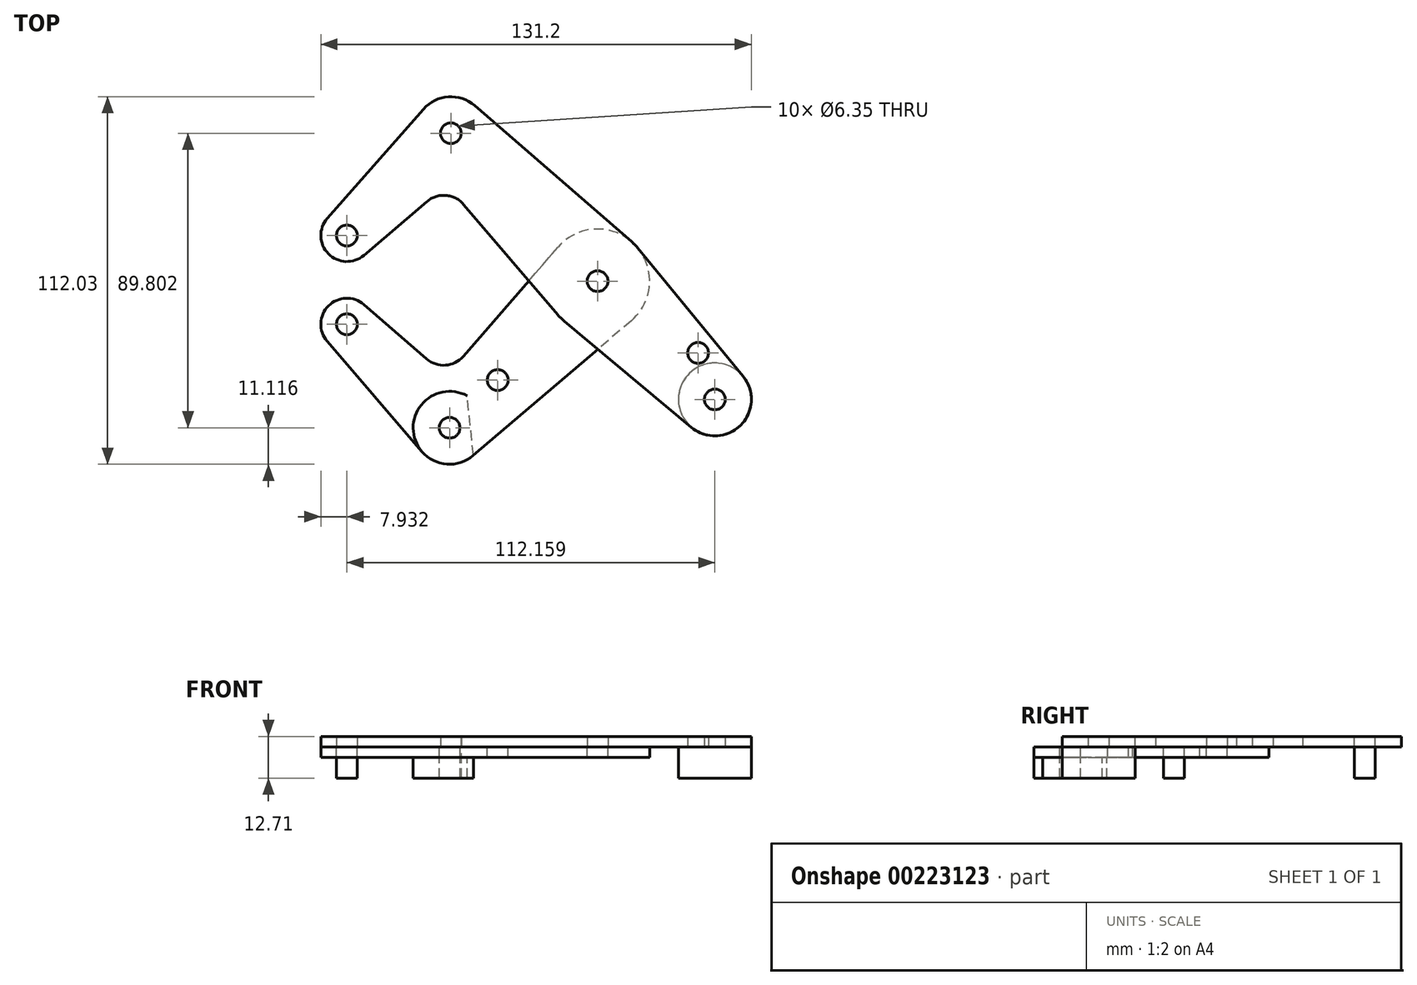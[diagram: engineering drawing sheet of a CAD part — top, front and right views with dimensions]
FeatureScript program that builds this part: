
annotation { "Feature Type Name" : "Feature", "Feature Type Description" : "" }
export const myFeature = defineFeature(function(context is Context, id is Id, definition is map)
    precondition{}
    {
        {
            var Q0;
            Q0=qCreatedBy(makeId("Top.planeOp"),FACE);
            var sketch = newSketch(context, id + "F0", { "sketchPlane" : qUnion([Q0])});
            skCircle(sketch, "E0", {"center": v(0, 0) * mm, "radius": 3.18 * mm});
            skCircle(sketch, "E1", {"center": v(0, 0) * mm, "radius": 3.98 * mm});
            skCircle(sketch, "E2", {"center": v(0, 0) * mm, "radius": 15.88 * mm});
            skCircle(sketch, "E3", {"center": v(35.77, -36.07) * mm, "radius": 11.11 * mm});
            skCircle(sketch, "E4", {"center": v(30.65, -21.9) * mm, "radius": 3.18 * mm});
            skCircle(sketch, "E5", {"center": v(-44.71, 45.09) * mm, "radius": 11.11 * mm});
            skCircle(sketch, "E6", {"center": v(-44.71, 45.09) * mm, "radius": 3.18 * mm});
            skCircle(sketch, "E7", {"center": v(-76.39, 13.9) * mm, "radius": 3.18 * mm});
            skCircle(sketch, "E8", {"center": v(-76.39, 13.9) * mm, "radius": 7.94 * mm});
            skCircle(sketch, "E9", {"center": v(-30.42, -30.17) * mm, "radius": 3.18 * mm});
            skCircle(sketch, "E10", {"center": v(-45.09, -44.71) * mm, "radius": 11.11 * mm});
            skCircle(sketch, "E11", {"center": v(-45.09, -44.71) * mm, "radius": 3.18 * mm});
            skCircle(sketch, "E12", {"center": v(-76.39, -13.15) * mm, "radius": 7.94 * mm});
            skCircle(sketch, "E13", {"center": v(-76.39, -13.15) * mm, "radius": 3.18 * mm});
            skLineSegment(sketch, "E14", {"start": v(-82.35, 19.14) * mm, "end": v(-53.06, 52.43) * mm});
            skLineSegment(sketch, "E15", {"start": v(-37.43, 53.48) * mm, "end": v(10.4, 12) * mm});
            skLineSegment(sketch, "E16", {"start": v(12.27, 10.07) * mm, "end": v(44.36, -29.02) * mm});
            skLineSegment(sketch, "E17", {"start": v(28.65, -44.6) * mm, "end": v(-10.17, -12.19) * mm});
            skLineSegment(sketch, "E18", {"start": v(10.3, -12.08) * mm, "end": v(-37.88, -53.17) * mm});
            skLineSegment(sketch, "E19", {"start": v(-40.89, -22.91) * mm, "end": v(-12, 10.4) * mm});
            skArc(sketch, "E20", {"start": v(-52, 24.26) * mm, "mid": v(-46.22, 26.14) * mm, "end": v(-40.8, 23.37) * mm});
            skLineSegment(sketch, "E21.trimOffspring", {"start": v(-40.8, 23.37) * mm, "end": v(-12.08, -10.3) * mm});
            skArc(sketch, "E22", {"start": v(-52.1, -23.7) * mm, "mid": v(-46.33, -25.63) * mm, "end": v(-40.89, -22.91) * mm});
            skLineSegment(sketch, "E23", {"start": v(0, 0) * mm, "end": v(-45.09, -44.71) * mm, "construction": true});
            skLineSegment(sketch, "E24", {"start": v(-45.09, -44.71) * mm, "end": v(-76.39, -13.15) * mm, "construction": true});
            skLineSegment(sketch, "E25", {"start": v(-44.71, 45.09) * mm, "end": v(-76.39, 13.9) * mm, "construction": true});
            skLineSegment(sketch, "E26", {"start": v(-76.39, 13.9) * mm, "end": v(-76.39, -13.15) * mm, "construction": true});
            skCircle(sketch, "E27", {"center": v(35.77, -36.07) * mm, "radius": 3.18 * mm});
            skLineSegment(sketch, "E28", {"start": v(-53.52, -51.96) * mm, "end": v(-82.4, -18.33) * mm});
            skLineSegment(sketch, "E29", {"start": v(-71.19, -7.16) * mm, "end": v(-52.1, -23.7) * mm});
            skLineSegment(sketch, "E30", {"start": v(-44.71, 45.09) * mm, "end": v(35.77, -36.07) * mm, "construction": true});
            skLineSegment(sketch, "E31", {"start": v(-52, 24.26) * mm, "end": v(-71.24, 7.86) * mm});
            skSolve(sketch);
        }
        {
            var Q0;
            {var subQ0=sQuery(id+"F0.wireOp",EDGE,"E14");Q0=makeQuery(id+"F0.imprint","IMPRINT",FACE,{"disambiguationData":[TD([[makeQuery(id+"F0.imprint","IMPRINT",EDGE,{"derivedFrom":subQ0}),-1.0]])]});}
            var Q1;
            Q1=makeQuery(id+"F0.imprint","IMPRINT",FACE,{"disambiguationData":[TD([[makeQuery(id+"F0.imprint","IMPRINT",EDGE,{"derivedFrom":sQuery(id+"F0.wireOp",EDGE,"E1")}),-1.0]])]});
            var Q2;
            Q2=makeQuery(id+"F0.imprint","IMPRINT",FACE,{"disambiguationData":[TD([[makeQuery(id+"F0.imprint","IMPRINT",EDGE,{"derivedFrom":sQuery(id+"F0.wireOp",EDGE,"E4")}),-1.0]])]});
            var Q3;
            Q3=makeQuery(id+"F0.imprint","IMPRINT",FACE,{"disambiguationData":[TD([[makeQuery(id+"F0.imprint","IMPRINT",EDGE,{"derivedFrom":sQuery(id+"F0.wireOp",EDGE,"E27")}),-1.0]])]});
            var Q4;
            Q4=makeQuery(id+"F0.imprint","IMPRINT",FACE,{"disambiguationData":[TD([[makeQuery(id+"F0.imprint","IMPRINT",EDGE,{"derivedFrom":sQuery(id+"F0.wireOp",EDGE,"E6")}),-1.0]])]});
            var Q5;
            Q5=makeQuery(id+"F0.imprint","IMPRINT",FACE,{"disambiguationData":[TD([[makeQuery(id+"F0.imprint","IMPRINT",EDGE,{"derivedFrom":sQuery(id+"F0.wireOp",EDGE,"E7")}),-1.0]])]});
            var Q6;
            {var subQ0=sQuery(id+"F0.wireOp",EDGE,"E19");var subQ1=sQuery(id+"F0.wireOp",EDGE,"E2");var subQ2=makeQuery(id+"F0.imprint","INTERSECT",VERTEX,{"derivedFrom":[subQ1,subQ0]});Q6=makeQuery(id+"F0.imprint","IMPRINT",FACE,{"disambiguationData":[TD([[makeQuery(id+"F0.imprint","IMPRINT",EDGE,{"disambiguationData":[TD([[subQ2,-1.0]])],"derivedFrom":subQ1}),-1.0]])]});}
            var Q7;
            {var subQ0=sQuery(id+"F0.wireOp",EDGE,"E17");var subQ1=sQuery(id+"F0.wireOp",EDGE,"E2");var subQ2=makeQuery(id+"F0.imprint","INTERSECT",VERTEX,{"derivedFrom":[subQ1,subQ0]});Q7=makeQuery(id+"F0.imprint","IMPRINT",FACE,{"disambiguationData":[TD([[makeQuery(id+"F0.imprint","IMPRINT",EDGE,{"disambiguationData":[TD([[subQ2,-1.0]])],"derivedFrom":subQ1}),-1.0]])]});}
            var Q8;
            Q8=makeQuery(id+"F0.imprint","IMPRINT",FACE,{"disambiguationData":[TD([[makeQuery(id+"F0.imprint","IMPRINT",EDGE,{"derivedFrom":sQuery(id+"F0.wireOp",EDGE,"E0")}),-1.0]])]});
            extrude(context, id + "F1", {"entities" : qUnion([Q0, Q1, Q2, Q3, Q4, Q5, Q6, Q7, Q8]), "depth" : 3.17 * mm});
        }
        {
            var Q0;
            Q0=makeQuery(id+"F0.imprint","IMPRINT",FACE,{"disambiguationData":[TD([[makeQuery(id+"F0.imprint","IMPRINT",EDGE,{"derivedFrom":sQuery(id+"F0.wireOp",EDGE,"E9")}),-1.0]])]});
            var Q1;
            Q1=makeQuery(id+"F0.imprint","IMPRINT",FACE,{"disambiguationData":[TD([[makeQuery(id+"F0.imprint","IMPRINT",EDGE,{"derivedFrom":sQuery(id+"F0.wireOp",EDGE,"E11")}),-1.0]])]});
            var Q2;
            Q2=makeQuery(id+"F0.imprint","IMPRINT",FACE,{"disambiguationData":[TD([[makeQuery(id+"F0.imprint","IMPRINT",EDGE,{"derivedFrom":sQuery(id+"F0.wireOp",EDGE,"E13")}),-1.0]])]});
            var Q3;
            Q3=makeQuery(id+"F0.imprint","IMPRINT",FACE,{"disambiguationData":[TD([[makeQuery(id+"F0.imprint","IMPRINT",EDGE,{"derivedFrom":sQuery(id+"F0.wireOp",EDGE,"E1")}),-1.0]])]});
            var Q4;
            {var subQ0=sQuery(id+"F0.wireOp",EDGE,"E19");var subQ1=sQuery(id+"F0.wireOp",EDGE,"E2");var subQ2=makeQuery(id+"F0.imprint","INTERSECT",VERTEX,{"derivedFrom":[subQ1,subQ0]});Q4=makeQuery(id+"F0.imprint","IMPRINT",FACE,{"disambiguationData":[TD([[makeQuery(id+"F0.imprint","IMPRINT",EDGE,{"disambiguationData":[TD([[subQ2,-1.0]])],"derivedFrom":subQ1}),-1.0]])]});}
            var Q5;
            {var subQ0=sQuery(id+"F0.wireOp",EDGE,"E17");var subQ1=sQuery(id+"F0.wireOp",EDGE,"E2");var subQ2=makeQuery(id+"F0.imprint","INTERSECT",VERTEX,{"derivedFrom":[subQ1,subQ0]});Q5=makeQuery(id+"F0.imprint","IMPRINT",FACE,{"disambiguationData":[TD([[makeQuery(id+"F0.imprint","IMPRINT",EDGE,{"disambiguationData":[TD([[subQ2,-1.0]])],"derivedFrom":subQ1}),-1.0]])]});}
            var Q6;
            Q6=makeQuery(id+"F0.imprint","IMPRINT",FACE,{"disambiguationData":[TD([[makeQuery(id+"F0.imprint","IMPRINT",EDGE,{"derivedFrom":sQuery(id+"F0.wireOp",EDGE,"E0")}),-1.0]])]});
            extrude(context, id + "F2", {"entities" : qUnion([Q0, Q1, Q2, Q3, Q4, Q5, Q6]), "oppositeDirection" : true, "depth" : 3.17 * mm});
        }
        {
            var Q0;
            Q0=makeQuery(id+"F1.opExtrude","CAP_FACE",FACE,{"disambiguationData":[OSD([sQuery(id+"F0.wireOp",EDGE,"E0"),sQuery(id+"F0.wireOp",EDGE,"E2"),sQuery(id+"F0.wireOp",EDGE,"E3"),sQuery(id+"F0.wireOp",EDGE,"E4"),sQuery(id+"F0.wireOp",EDGE,"E5"),sQuery(id+"F0.wireOp",EDGE,"E6"),sQuery(id+"F0.wireOp",EDGE,"E7"),sQuery(id+"F0.wireOp",EDGE,"E8"),sQuery(id+"F0.wireOp",EDGE,"E14"),sQuery(id+"F0.wireOp",EDGE,"E15"),sQuery(id+"F0.wireOp",EDGE,"E16"),sQuery(id+"F0.wireOp",EDGE,"E17"),sQuery(id+"F0.wireOp",EDGE,"E20"),sQuery(id+"F0.wireOp",EDGE,"E21.trimOffspring"),sQuery(id+"F0.wireOp",EDGE,"E27"),sQuery(id+"F0.wireOp",EDGE,"E31")])],"isStart":false});
            var sketch = newSketch(context, id + "F3", { "sketchPlane" : qUnion([Q0])});
            skCircle(sketch, "E32.0", {"center": v(35.77, -36.07) * mm, "radius": 11.11 * mm});
            skCircle(sketch, "E33.0", {"center": v(0, 0) * mm, "radius": 3.98 * mm});
            skCircle(sketch, "E34", {"center": v(-44.71, 45.09) * mm, "radius": 3.98 * mm});
            skSolve(sketch);
        }
        {
            var Q0;
            Q0=makeQuery(id+"F2.opExtrude","CAP_FACE",FACE,{"disambiguationData":[OSD([sQuery(id+"F0.wireOp",EDGE,"E0"),sQuery(id+"F0.wireOp",EDGE,"E2"),sQuery(id+"F0.wireOp",EDGE,"E9"),sQuery(id+"F0.wireOp",EDGE,"E10"),sQuery(id+"F0.wireOp",EDGE,"E11"),sQuery(id+"F0.wireOp",EDGE,"E12"),sQuery(id+"F0.wireOp",EDGE,"E13"),sQuery(id+"F0.wireOp",EDGE,"E18"),sQuery(id+"F0.wireOp",EDGE,"E19"),sQuery(id+"F0.wireOp",EDGE,"E22"),sQuery(id+"F0.wireOp",EDGE,"E28"),sQuery(id+"F0.wireOp",EDGE,"E29")])],"isStart":true});
            var sketch = newSketch(context, id + "F4", { "sketchPlane" : qUnion([Q0])});
            skCircle(sketch, "E35.0", {"center": v(-45.09, -44.71) * mm, "radius": 11.11 * mm});
            skPoint(sketch, "E36.0", {"position": v(35.77, -36.07) * mm});
            skLineSegment(sketch, "E37", {"start": v(35.77, -36.07) * mm, "end": v(-45.09, -44.71) * mm, "construction": true});
            skLineSegment(sketch, "E38", {"start": v(-39.74, -34.97) * mm, "end": v(-37.8, -53.1) * mm});
            skSolve(sketch);
        }
        {
            var Q0;
            Q0=qCreatedBy(makeId("Top.planeOp"),FACE);
            cPlane(context, id + "F5", {"entities" : qUnion([Q0]), "cplaneType" : CPlaneType.OFFSET, "offset" : 9.52 * mm, "oppositeDirection" : true, "width" : 152.4 * mm, "height" : 152.4 * mm});
        }
        {
            var Q0;
            Q0=makeQuery(id+"F0.imprint","IMPRINT",FACE,{"disambiguationData":[TD([[makeQuery(id+"F0.imprint","IMPRINT",EDGE,{"derivedFrom":sQuery(id+"F0.wireOp",EDGE,"E13")}),1.0]])]});
            var Q1;
            Q1=makeQuery(id+"F3.imprint","IMPRINT",FACE,{"disambiguationData":[TD([[makeQuery(id+"F3.imprint","IMPRINT",EDGE,{"derivedFrom":makeQuery(id+"F1.opExtrude","CAP_EDGE",EDGE,{"disambiguationData":[OSD([sQuery(id+"F0.wireOp",EDGE,"E6")])],"isStart":false})}),1.0]])]});
            var Q2;
            Q2=makeQuery(id+"F3.imprint","IMPRINT",FACE,{"disambiguationData":[TD([[makeQuery(id+"F3.imprint","IMPRINT",EDGE,{"derivedFrom":makeQuery(id+"F1.opExtrude","CAP_EDGE",EDGE,{"disambiguationData":[OSD([sQuery(id+"F0.wireOp",EDGE,"E27")])],"isStart":false})}),-1.0]])]});
            var Q3;
            Q3=makeQuery(id+"F3.imprint","IMPRINT",FACE,{"disambiguationData":[TD([[makeQuery(id+"F3.imprint","IMPRINT",EDGE,{"derivedFrom":makeQuery(id+"F1.opExtrude","CAP_EDGE",EDGE,{"disambiguationData":[OSD([sQuery(id+"F0.wireOp",EDGE,"E27")])],"isStart":false})}),1.0]])]});
            var Q4;
            Q4=qCreatedBy(id+"F5.planeOp",FACE);
            extrude(context, id + "F6", {"entities" : qUnion([Q0, Q1, Q2, Q3]), "endBound" : BoundingType.UP_TO_SURFACE, "oppositeDirection" : true, "endBoundEntityFace" : qUnion([Q4]), "depth" : 25.4 * mm});
        }
        {
            var Q0;
            {var subQ0=sQuery(id+"F4.wireOp",EDGE,"E38");Q0=makeQuery(id+"F4.imprint","IMPRINT",FACE,{"disambiguationData":[TD([[makeQuery(id+"F4.imprint","IMPRINT",EDGE,{"derivedFrom":subQ0}),-1.0]])]});}
            var Q1;
            Q1=makeQuery(id+"F0.imprint","IMPRINT",FACE,{"disambiguationData":[TD([[makeQuery(id+"F0.imprint","IMPRINT",EDGE,{"derivedFrom":sQuery(id+"F0.wireOp",EDGE,"E11")}),1.0]])]});
            var Q2;
            Q2=qCreatedBy(id+"F5.planeOp",FACE);
            extrude(context, id + "F7", {"entities" : qUnion([Q0, Q1]), "endBound" : BoundingType.UP_TO_SURFACE, "oppositeDirection" : true, "endBoundEntityFace" : qUnion([Q2]), "depth" : 25.4 * mm});
        }
        {
            var Q0;
            Q0=makeQuery(id+"F2.opExtrude","SWEPT_BODY",BODY,{"disambiguationData":[OSD([sQuery(id+"F0.wireOp",EDGE,"E0"),sQuery(id+"F0.wireOp",EDGE,"E2"),sQuery(id+"F0.wireOp",EDGE,"E9"),sQuery(id+"F0.wireOp",EDGE,"E10"),sQuery(id+"F0.wireOp",EDGE,"E11"),sQuery(id+"F0.wireOp",EDGE,"E12"),sQuery(id+"F0.wireOp",EDGE,"E13"),sQuery(id+"F0.wireOp",EDGE,"E18"),sQuery(id+"F0.wireOp",EDGE,"E19"),sQuery(id+"F0.wireOp",EDGE,"E22"),sQuery(id+"F0.wireOp",EDGE,"E28"),sQuery(id+"F0.wireOp",EDGE,"E29")])]});
            var Q1;
            Q1=makeQuery(id+"F7.opExtrude","SWEPT_BODY",BODY,{"disambiguationData":[OSD([sQuery(id+"F0.wireOp",EDGE,"E11"),sQuery(id+"F4.wireOp",EDGE,"E35.0"),sQuery(id+"F4.wireOp",EDGE,"E38")])]});
            var Q2;
            Q2=makeQuery(id+"F6.opExtrude","SWEPT_BODY",BODY,{"disambiguationData":[OSD([sQuery(id+"F0.wireOp",EDGE,"E13")])]});
            booleanBodies(context, id + "F8", {"operationType" : BooleanOperationType.SUBTRACTION, "tools" : qUnion([Q0]), "targets" : qUnion([Q1, Q2]), "keepTools" : true});
        }
        {
            var Q0;
            Q0=makeQuery(id+"F1.opExtrude","SWEPT_BODY",BODY,{"disambiguationData":[OSD([sQuery(id+"F0.wireOp",EDGE,"E0"),sQuery(id+"F0.wireOp",EDGE,"E2"),sQuery(id+"F0.wireOp",EDGE,"E3"),sQuery(id+"F0.wireOp",EDGE,"E4"),sQuery(id+"F0.wireOp",EDGE,"E5"),sQuery(id+"F0.wireOp",EDGE,"E6"),sQuery(id+"F0.wireOp",EDGE,"E7"),sQuery(id+"F0.wireOp",EDGE,"E8"),sQuery(id+"F0.wireOp",EDGE,"E14"),sQuery(id+"F0.wireOp",EDGE,"E15"),sQuery(id+"F0.wireOp",EDGE,"E16"),sQuery(id+"F0.wireOp",EDGE,"E17"),sQuery(id+"F0.wireOp",EDGE,"E20"),sQuery(id+"F0.wireOp",EDGE,"E21.trimOffspring"),sQuery(id+"F0.wireOp",EDGE,"E27"),sQuery(id+"F0.wireOp",EDGE,"E31")])]});
            var Q1;
            Q1=makeQuery(id+"F6.opExtrude","SWEPT_BODY",BODY,{"disambiguationData":[OSD([sQuery(id+"F3.wireOp",EDGE,"E32.0")])]});
            booleanBodies(context, id + "F9", {"operationType" : BooleanOperationType.SUBTRACTION, "tools" : qUnion([Q0]), "targets" : qUnion([Q1]), "keepTools" : true});
        }
    });
